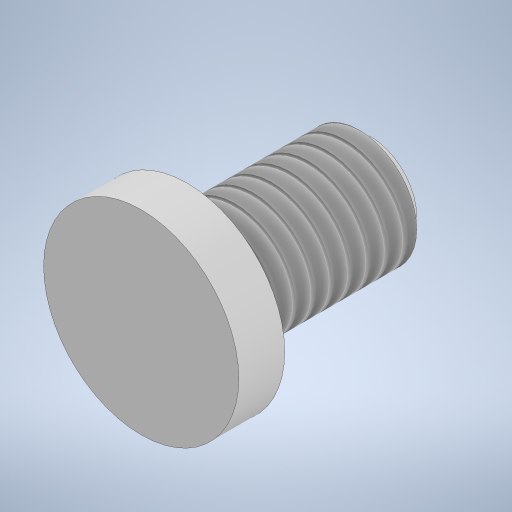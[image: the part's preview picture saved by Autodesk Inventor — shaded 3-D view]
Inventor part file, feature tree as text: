
AUTODESK INVENTOR PART (.ipt)
format: ipt  version: 2023 (Build 270158000, 158)  size: 257,536 bytes
history: native  units: mm
features: other x1, revolve x1, thread x1, chamfer x1, sketch x1
ambient origin geometry x8: Origin, YZ Plane, XZ Plane, XY Plane, X Axis, Y Axis, Z Axis, Center Point
bodies: Body1 (feature_tree)
feature tree (5):
  other  "Твердое тело1"
  revolve  "Вращение1"
  thread  "Резьба1"
  chamfer  "Фаска1"  Distance=4.25mm
  sketch  "Эскиз1"
